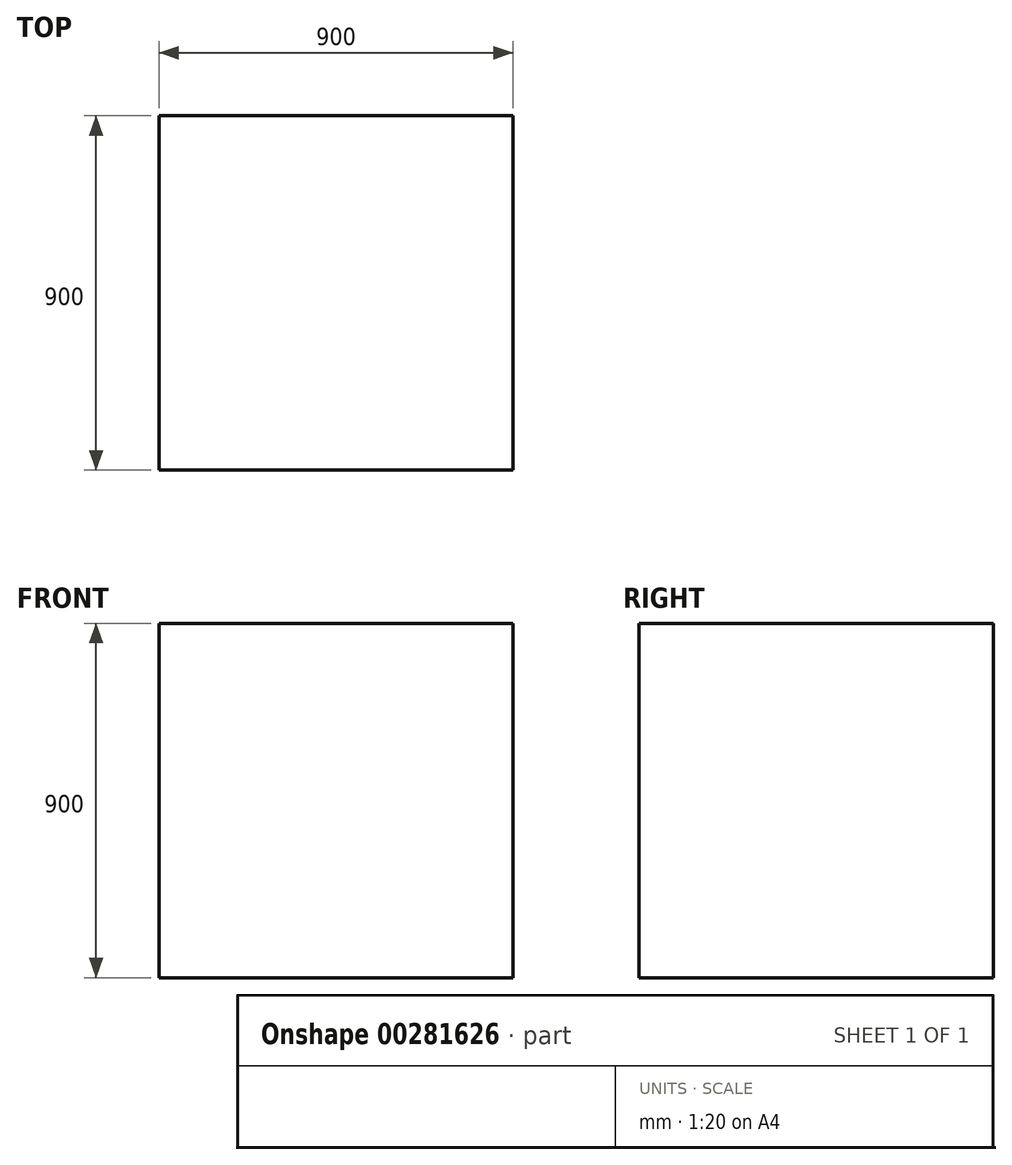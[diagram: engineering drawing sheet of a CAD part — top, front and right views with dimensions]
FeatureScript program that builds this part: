
annotation { "Feature Type Name" : "Feature", "Feature Type Description" : "" }
export const myFeature = defineFeature(function(context is Context, id is Id, definition is map)
    precondition{}
    {
        {
            var Q0;
            Q0=qCreatedBy(makeId("Top.planeOp"), FACE);
            var sketch = newSketch(context, id + "F0", { "sketchPlane" : qUnion([Q0])});
            skLineSegment(sketch, "E0.bottom", {"start": v(-50.96, 854.7) * mm, "end": v(849.04, 854.7) * mm});
            skLineSegment(sketch, "E0.top", {"start": v(-50.96, -45.3) * mm, "end": v(849.04, -45.3) * mm});
            skLineSegment(sketch, "E0.left", {"start": v(-50.96, 854.7) * mm, "end": v(-50.96, -45.3) * mm});
            skLineSegment(sketch, "E0.right", {"start": v(849.04, 854.7) * mm, "end": v(849.04, -45.3) * mm});
            skSolve(sketch);
        }
        {
            var Q0;
            Q0 = qSketchRegion(id + "F0", true);
            extrude(context, id + "F1", {"entities" : qUnion([Q0]), "depth" : 900 * mm, "offsetDistance" : 25 * mm});
        }
    });
